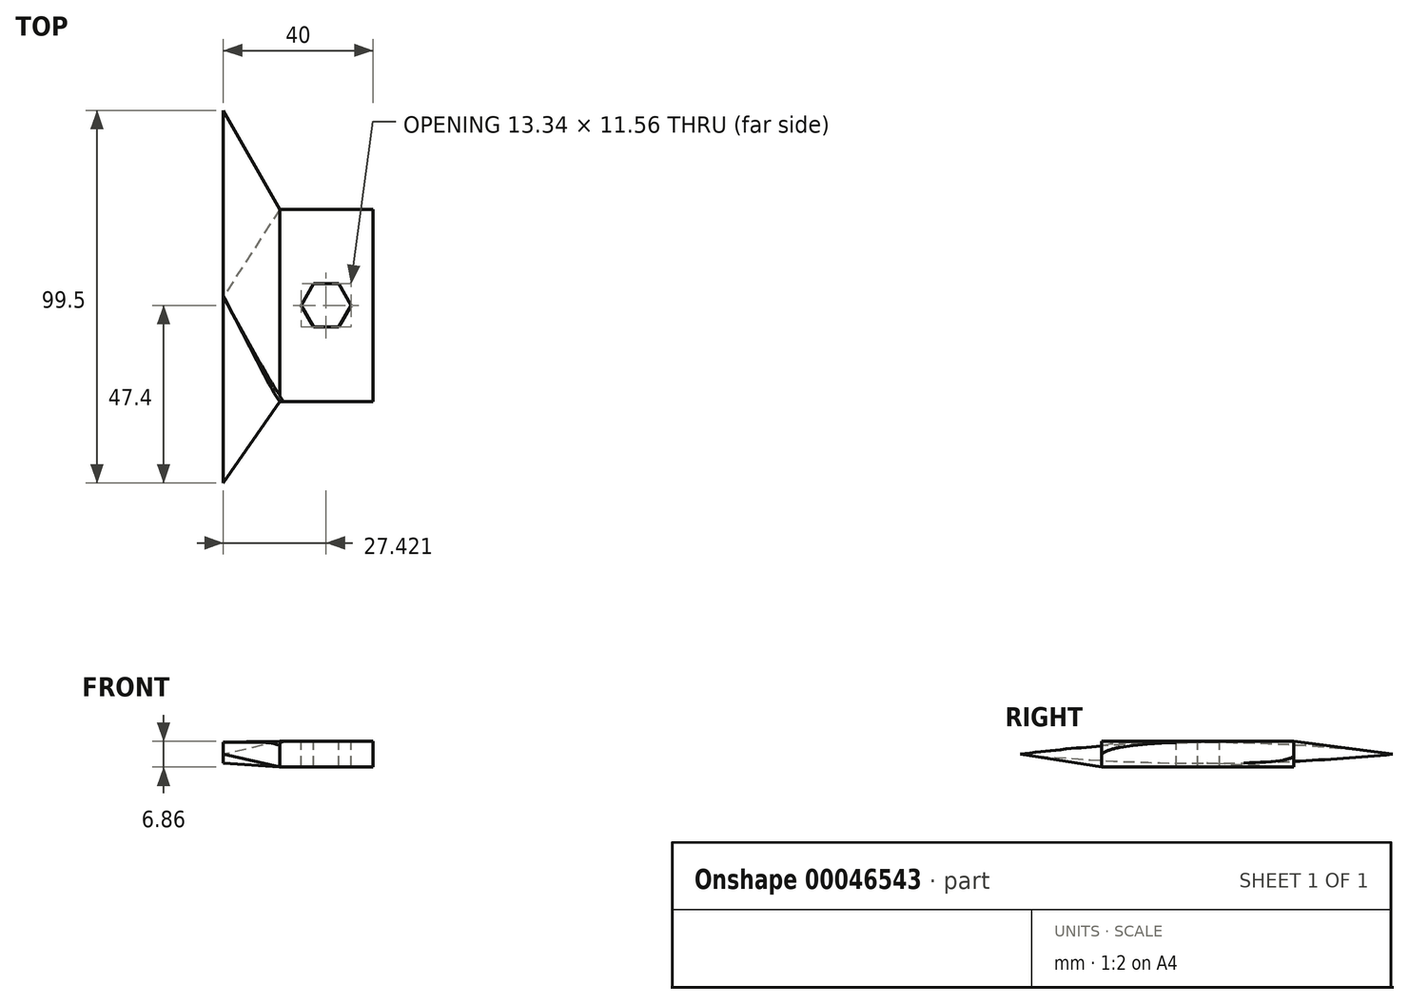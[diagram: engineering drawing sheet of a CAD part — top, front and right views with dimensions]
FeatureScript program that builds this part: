
annotation { "Feature Type Name" : "Feature", "Feature Type Description" : "" }
export const myFeature = defineFeature(function(context is Context, id is Id, definition is map)
    precondition{}
    {
        {
            var Q0;
            Q0=qCreatedBy(makeId("Right.planeOp"),FACE);
            var sketch = newSketch(context, id + "F0", { "sketchPlane" : qUnion([Q0])});
            skArc(sketch, "E0", {"start": v(52.1, 0) * mm, "mid": v(2.35, 3.2) * mm, "end": v(-47.4, 0) * mm});
            skArc(sketch, "E1", {"start": v(-47.4, 0) * mm, "mid": v(2.35, -2.4) * mm, "end": v(52.1, 0) * mm});
            skSolve(sketch);
        }
        {
            var Q0;
            Q0=qCreatedBy(makeId("Right.planeOp"),FACE);
            cPlane(context, id + "F1", {"entities" : qUnion([Q0]), "cplaneType" : CPlaneType.OFFSET, "offset" : 15 * mm, "width" : 152.4 * mm, "height" : 152.4 * mm});
        }
        {
            var Q0;
            Q0=qCreatedBy(id+"F1.planeOp",FACE);
            var sketch = newSketch(context, id + "F2", { "sketchPlane" : qUnion([Q0])});
            skLineSegment(sketch, "E2.rect.bottom", {"start": v(-25.65, -3.42) * mm, "end": v(25.65, -3.42) * mm});
            skLineSegment(sketch, "E2.rect.top", {"start": v(-25.65, 3.42) * mm, "end": v(25.65, 3.42) * mm});
            skLineSegment(sketch, "E2.rect.left", {"start": v(-25.65, -3.42) * mm, "end": v(-25.65, 3.42) * mm});
            skLineSegment(sketch, "E2.rect.right", {"start": v(25.65, -3.42) * mm, "end": v(25.65, 3.42) * mm});
            skPoint(sketch, "E2.rect.middle", {"position": v(0, 0) * mm});
            skSolve(sketch);
        }
        {
            var Q0;
            Q0=makeQuery(id+"F2.imprint","IMPRINT",FACE,{"disambiguationData":[TD([[makeQuery(id+"F2.imprint","IMPRINT",EDGE,{"derivedFrom":sQuery(id+"F2.wireOp",EDGE,"E2.rect.bottom")}),1.0]])]});
            extrude(context, id + "F3", {"entities" : qUnion([Q0]), "depth" : 25 * mm});
        }
        {
            var Q0;
            Q0=makeQuery(id+"F3.opExtrude","SWEPT_FACE",FACE,{"disambiguationData":[OSD([sQuery(id+"F2.wireOp",EDGE,"E2.rect.top")])]});
            var sketch = newSketch(context, id + "F4", { "sketchPlane" : qUnion([Q0])});
            skCircle(sketch, "E3.cCircle", {"center": v(27.42, 0) * mm, "radius": 5.78 * mm, "construction": true});
            skLineSegment(sketch, "E3.0", {"start": v(24.08, 5.78) * mm, "end": v(30.76, 5.78) * mm});
            skLineSegment(sketch, "E3.1", {"start": v(30.76, 5.78) * mm, "end": v(34.1, 0) * mm});
            skLineSegment(sketch, "E3.2", {"start": v(34.1, 0) * mm, "end": v(30.76, -5.78) * mm});
            skLineSegment(sketch, "E3.3", {"start": v(30.76, -5.78) * mm, "end": v(24.08, -5.78) * mm});
            skLineSegment(sketch, "E3.4", {"start": v(24.08, -5.78) * mm, "end": v(20.75, 0) * mm});
            skLineSegment(sketch, "E3.5", {"start": v(20.75, 0) * mm, "end": v(24.08, 5.78) * mm});
            skPoint(sketch, "E3.0.midPoint", {"position": v(27.42, 5.78) * mm});
            skSolve(sketch);
        }
        {
            var Q0;
            Q0=makeQuery(id+"F4.imprint","IMPRINT",FACE,{"disambiguationData":[TD([[makeQuery(id+"F4.imprint","IMPRINT",EDGE,{"derivedFrom":sQuery(id+"F4.wireOp",EDGE,"E3.0")}),-1.0]])]});
            extrude(context, id + "F5", {"entities" : qUnion([Q0]), "operationType" : NewBodyOperationType.REMOVE, "oppositeDirection" : true, "depth" : 25 * mm});
        }
        {
            var Q1;
            Q1=makeQuery(id+"F3.opExtrude","CAP_FACE",FACE,{"disambiguationData":[OSD([sQuery(id+"F2.wireOp",EDGE,"E2.rect.bottom"),sQuery(id+"F2.wireOp",EDGE,"E2.rect.top"),sQuery(id+"F2.wireOp",EDGE,"E2.rect.left"),sQuery(id+"F2.wireOp",EDGE,"E2.rect.right")])],"isStart":true});
            var Q2;
            Q2=makeQuery(id+"F0.imprint","IMPRINT",FACE,{"disambiguationData":[TD([[makeQuery(id+"F0.imprint","IMPRINT",EDGE,{"derivedFrom":sQuery(id+"F0.wireOp",EDGE,"E0")}),1.0]])]});
            loft(context, id + "F6", {"operationType" : NewBodyOperationType.ADD, "sheetProfilesArray" : [{ "sheetProfileEntities" : qUnion([Q1]) }, { "sheetProfileEntities" : qUnion([Q2]) }]});
        }
        {
            var Q0;
            Q0=makeQuery(id+"F6.opLoft","SWEPT_EDGE",EDGE,{"disambiguationData":[OSD([sQuery(id+"F0.wireOp",EDGE,"E0"),sQuery(id+"F2.wireOp",EDGE,"E2.rect.top"),sQuery(id+"F2.wireOp",EDGE,"E2.rect.left"),sQuery(id+"F2.wireOp",EDGE,"E2.rect.right")])]});
            var Q1;
            Q1=makeQuery(id+"F6.opLoft","SWEPT_EDGE",EDGE,{"disambiguationData":[OSD([sQuery(id+"F0.wireOp",EDGE,"E0"),sQuery(id+"F2.wireOp",EDGE,"E2.rect.bottom"),sQuery(id+"F2.wireOp",EDGE,"E2.rect.top"),sQuery(id+"F2.wireOp",EDGE,"E2.rect.left")])]});
            fillet(context, id + "F7", {"entities" : qUnion([Q0, Q1]), "radius" : 1 * mm, "tangentPropagation" : true, "allowEdgeOverflow" : false});
        }
    });
